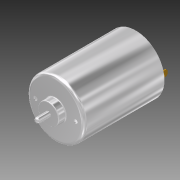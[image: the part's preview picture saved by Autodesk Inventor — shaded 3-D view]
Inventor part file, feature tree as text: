
AUTODESK INVENTOR PART (.ipt)
format: ipt  version: 2012 (Build 160160000, 160)  size: 232,960 bytes
history: native  units: mm (DEFAULTED — no unit token found)
features: sketch x12, extrude x10, fillet x3, hole x2, mirror x2, shell x1, plane x1, pattern_circular x1, chamfer x1
ambient origin geometry x8: Origin, YZ Plane, XZ Plane, XY Plane, X Axis, Y Axis, Z Axis, Center Point
bodies: Solid1 (feature_tree)
feature tree (33):
  extrude  "Extrusion1"  Depth=50.0mm TaperAngle=0.0deg
  fillet  "Fillet1"  Radius=2.0mm
  shell  "Shell1"  Thickness=0.62mm
  extrude  "Extrusion2"  Depth=4.5mm TaperAngle=0.0deg
  fillet  "Fillet2"  Radius=0.5mm
  extrude  "Extrusion3"  Depth=8.0mm TaperAngle=0.0deg
  fillet  "Fillet3"  Radius=1.6mm
  hole  "Hole1"  [1 undecoded]
  mirror  "Mirror1"
  plane  "Work Plane1"
  extrude  "Extrusion5"  Depth=24.0mm
  extrude  "Extrusion6"  Depth=10.75mm
  extrude  "Extrusion7"  Depth=6.9mm
  extrude  "Extrusion8"  Depth=3.2mm
  extrude  "Extrusion9"  Depth=3.15mm
  extrude  "Extrusion10"  Depth=9.75mm
  pattern_circular  "Circular Pattern2"  [2 undecoded]
  extrude  "Extrusion11"  Depth=40.0mm TaperAngle=360.0deg
  chamfer  "Chamfer1"  Distance=0.5mm
  hole  "Hole2"  [1 undecoded]
  mirror  "Mirror2"
  sketch  "Sketch1"  dims[d0=35.75mm d1=50.0mm d2=0.0mm d3=2.0mm d4=0.62mm]
  sketch  "Sketch2"  dims[d5=13.0mm d6=4.5mm d7=0.0mm d8=0.5mm]
  sketch  "Sketch3"  dims[d9=3.2mm d10=8.0mm d11=0.0mm d12=1.6mm]
  sketch  "Sketch4"  dims[d13=12.5mm]
  sketch  "Sketch6"  dims[d14=2.5mm d15=6.0mm d16=4.0mm d17=2.0mm d18=14.3117mm d19=8.0mm d20=20.594885mm d30=-1.75mm]
  sketch  "Sketch7"  dims[d31=0.62mm d32=0.0mm d33=24.0mm]
  sketch  "Sketch8"  dims[d34=0.62mm d35=0.0mm d36=10.75mm]
  sketch  "Sketch9"  dims[d37=3.0mm d38=0.0mm d39=6.9mm]
  sketch  "Sketch10"  dims[d40=0.8mm d41=0.0mm d42=3.2mm]
  sketch  "Sketch11"  dims[d43=1.0mm d44=0.0mm d45=3.15mm]
  sketch  "Sketch12"  dims[d46=3.15mm d47=9.75mm]
  sketch  "Sketch13"  dims[d48=8.75mm d49=1.0mm d50=0.0mm d51=40.0mm d53=360.0deg d54=0.5mm d55=3.8mm d56=14.0mm d57=7.2mm d58=0.0mm d59=1.0mm d60=2.0mm d61=3.0mm d62=2.0mm d63=6.0mm d64=4.0mm d65=2.0mm d66=14.3117mm d67=1.0mm d68=20.594885mm d75=45.0deg]
note: 4 required parameter values undecoded (feature->parameter linkage not recoverable at this tier; creation-order binding heuristic only, values carry confidence <= 0.55)
